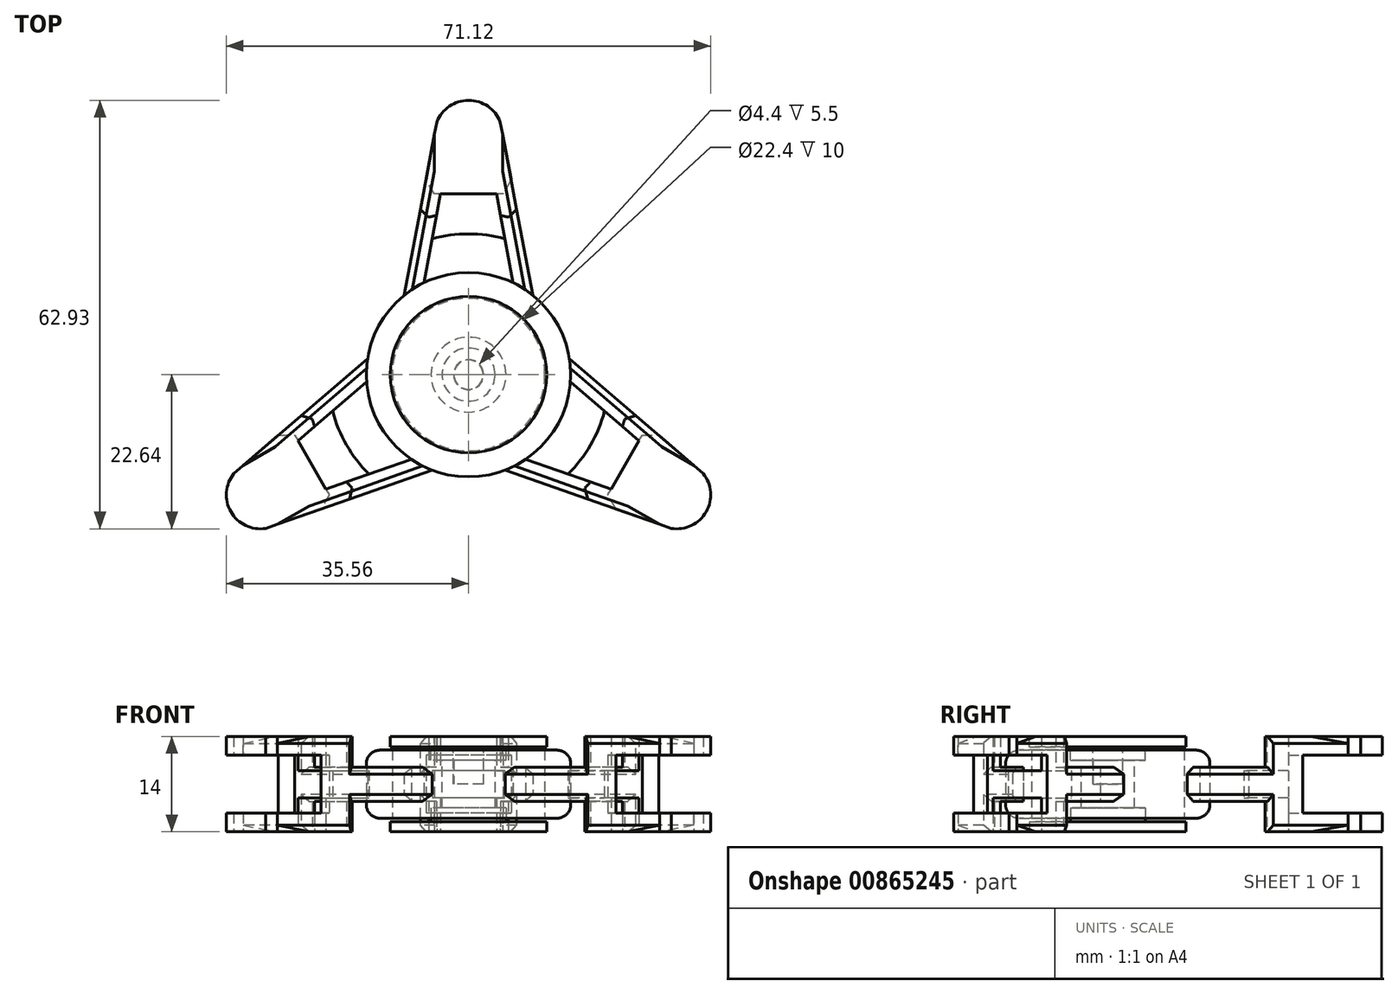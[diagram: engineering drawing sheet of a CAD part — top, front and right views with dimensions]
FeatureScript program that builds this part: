
annotation { "Feature Type Name" : "Feature", "Feature Type Description" : "" }
export const myFeature = defineFeature(function(context is Context, id is Id, definition is map)
    precondition{}
    {
        {
            var Q0;
            Q0=qCreatedBy(makeId("Top.planeOp"),FACE);
            var sketch = newSketch(context, id + "F0", { "sketchPlane" : qUnion([Q0])});
            skCircle(sketch, "E0", {"center": v(0, 0) * mm, "radius": 11.2 * mm});
            skCircle(sketch, "E1", {"center": v(0, 0) * mm, "radius": 15 * mm});
            skLineSegment(sketch, "E2.bottom", {"start": v(-1.99, 37.79) * mm, "end": v(1.99, 37.79) * mm});
            skLineSegment(sketch, "E2.top", {"start": v(-6.99, 11.2) * mm, "end": v(6.99, 11.2) * mm});
            skLineSegment(sketch, "E2.left", {"start": v(-1.99, 37.79) * mm, "end": v(-6.99, 11.2) * mm});
            skLineSegment(sketch, "E2.right", {"start": v(1.99, 37.79) * mm, "end": v(6.99, 11.2) * mm});
            skLineSegment(sketch, "E3.0", {"start": v(-4.06, 40.29) * mm, "end": v(-10, 8.7) * mm});
            skLineSegment(sketch, "E3.1", {"start": v(-4.06, 40.29) * mm, "end": v(4.06, 40.29) * mm});
            skLineSegment(sketch, "E3.2", {"start": v(4.06, 40.29) * mm, "end": v(10, 8.7) * mm});
            skLineSegment(sketch, "E3.3", {"start": v(-10, 8.7) * mm, "end": v(10, 8.7) * mm});
            skCircle(sketch, "E4", {"center": v(0, 0) * mm, "radius": 20.67 * mm});
            skCircle(sketch, "E5", {"center": v(0, 35.29) * mm, "radius": 5 * mm});
            skLineSegment(sketch, "E6", {"start": v(-30.4, 35.29) * mm, "end": v(24.87, 35.29) * mm});
            skCircle(sketch, "E7", {"center": v(0, 35.29) * mm, "radius": 2.3 * mm});
            skCircle(sketch, "E8", {"center": v(0, 35.29) * mm, "radius": 4.5 * mm});
            skCircle(sketch, "E9.cCircle", {"center": v(0, 35.29) * mm, "radius": 8.75 * mm, "construction": true});
            skLineSegment(sketch, "E9.0", {"start": v(10.1, 35.29) * mm, "end": v(5.05, 26.54) * mm});
            skLineSegment(sketch, "E9.1", {"start": v(5.05, 26.54) * mm, "end": v(-5.05, 26.54) * mm});
            skLineSegment(sketch, "E9.2", {"start": v(-5.05, 26.54) * mm, "end": v(-10.1, 35.29) * mm});
            skLineSegment(sketch, "E9.3", {"start": v(-10.1, 35.29) * mm, "end": v(-5.05, 44.04) * mm});
            skLineSegment(sketch, "E9.4", {"start": v(-5.05, 44.04) * mm, "end": v(5.05, 44.04) * mm});
            skLineSegment(sketch, "E9.5", {"start": v(5.05, 44.04) * mm, "end": v(10.1, 35.29) * mm});
            skPoint(sketch, "E9.0.midPoint", {"position": v(7.58, 30.91) * mm});
            skCircle(sketch, "E10", {"center": v(0, 0) * mm, "radius": 23.85 * mm});
            skCircle(sketch, "E11", {"center": v(0, 35.29) * mm, "radius": 3.2 * mm});
            skSolve(sketch);
        }
        {
            var Q0;
            {var subQ3=sQuery(id+"F0.wireOp",EDGE,"E0");Q0=makeQuery(id+"F0.imprint","IMPRINT",FACE,{"disambiguationData":[TD([[makeQuery(id+"F0.imprint","IMPRINT",EDGE,{"derivedFrom":subQ3}),-1.0]])]});}
            var Q1;
            {var subQ0=sQuery(id+"F0.wireOp",EDGE,"E2.left");var subQ3=sQuery(id+"F0.wireOp",EDGE,"E1");var subQ4=makeQuery(id+"F0.imprint","INTERSECT",VERTEX,{"derivedFrom":[subQ3,subQ0]});Q1=makeQuery(id+"F0.imprint","IMPRINT",FACE,{"disambiguationData":[TD([[makeQuery(id+"F0.imprint","IMPRINT",EDGE,{"disambiguationData":[TD([[subQ4,1.0]])],"derivedFrom":subQ3}),1.0]])]});}
            var Q2;
            {var subQ3=sQuery(id+"F0.wireOp",EDGE,"E1");var subQ6=sQuery(id+"F0.wireOp",EDGE,"c8613fa5-9237-46bb-8146-0ead7ceadabf.1.1");var subQ8=makeQuery(id+"F0.imprint","INTERSECT",VERTEX,{"derivedFrom":[subQ3,subQ6]});Q2=makeQuery(id+"F0.imprint","IMPRINT",FACE,{"disambiguationData":[TD([[makeQuery(id+"F0.imprint","IMPRINT",EDGE,{"disambiguationData":[TD([[subQ8,-1.0]])],"derivedFrom":subQ3}),1.0]])]});}
            var Q3;
            {var subQ3=sQuery(id+"F0.wireOp",EDGE,"E1");var subQ6=sQuery(id+"F0.wireOp",EDGE,"c8613fa5-9237-46bb-8146-0ead7ceadabf.2.1");var subQ8=makeQuery(id+"F0.imprint","INTERSECT",VERTEX,{"derivedFrom":[subQ3,subQ6]});Q3=makeQuery(id+"F0.imprint","IMPRINT",FACE,{"disambiguationData":[TD([[makeQuery(id+"F0.imprint","IMPRINT",EDGE,{"disambiguationData":[TD([[subQ8,-1.0]])],"derivedFrom":subQ3}),1.0]])]});}
            extrude(context, id + "F1", {"entities" : qUnion([Q0, Q1, Q2, Q3]), "endBound" : BoundingType.SYMMETRIC, "depth" : 10 * mm, "offsetDistance" : 25 * mm});
        }
        {
            var Q0;
            {var subQ0=sQuery(id+"F0.wireOp",EDGE,"E2.right");var subQ1=sQuery(id+"F0.wireOp",EDGE,"E1");var subQ2=makeQuery(id+"F0.imprint","INTERSECT",VERTEX,{"derivedFrom":[subQ1,subQ0]});Q0=makeQuery(id+"F0.imprint","IMPRINT",FACE,{"disambiguationData":[TD([[makeQuery(id+"F0.imprint","IMPRINT",EDGE,{"disambiguationData":[TD([[subQ2,1.0]])],"derivedFrom":subQ1}),-1.0]])]});}
            var Q1;
            {var subQ0=sQuery(id+"F0.wireOp",EDGE,"E2.left");var subQ1=sQuery(id+"F0.wireOp",EDGE,"E1");var subQ2=makeQuery(id+"F0.imprint","INTERSECT",VERTEX,{"derivedFrom":[subQ1,subQ0]});Q1=makeQuery(id+"F0.imprint","IMPRINT",FACE,{"disambiguationData":[TD([[makeQuery(id+"F0.imprint","IMPRINT",EDGE,{"disambiguationData":[TD([[subQ2,-1.0]])],"derivedFrom":subQ1}),-1.0]])]});}
            var Q2;
            {var subQ0=sQuery(id+"F0.wireOp",EDGE,"E10");var subQ1=sQuery(id+"F0.wireOp",EDGE,"E2.left");var subQ2=makeQuery(id+"F0.imprint","INTERSECT",VERTEX,{"derivedFrom":[subQ1,subQ0]});Q2=makeQuery(id+"F0.imprint","IMPRINT",FACE,{"disambiguationData":[TD([[makeQuery(id+"F0.imprint","IMPRINT",EDGE,{"disambiguationData":[TD([[subQ2,-1.0]])],"derivedFrom":subQ1}),-1.0]])]});}
            var Q3;
            {var subQ0=sQuery(id+"F0.wireOp",EDGE,"E10");var subQ1=sQuery(id+"F0.wireOp",EDGE,"E2.right");var subQ2=makeQuery(id+"F0.imprint","INTERSECT",VERTEX,{"derivedFrom":[subQ1,subQ0]});Q3=makeQuery(id+"F0.imprint","IMPRINT",FACE,{"disambiguationData":[TD([[makeQuery(id+"F0.imprint","IMPRINT",EDGE,{"disambiguationData":[TD([[subQ2,-1.0]])],"derivedFrom":subQ1}),1.0]])]});}
            extrude(context, id + "F2", {"entities" : qUnion([Q0, Q1, Q2, Q3]), "endBound" : BoundingType.SYMMETRIC, "depth" : 5 * mm, "offsetDistance" : 25 * mm});
        }
        {
            var Q0;
            {var subQ0=sQuery(id+"F0.wireOp",EDGE,"76ec63e9-d2f9-4aa1-b3ab-0722a41de434.2.0");var subQ1=sQuery(id+"F0.wireOp",EDGE,"c8613fa5-9237-46bb-8146-0ead7ceadabf.2.1");var subQ2=makeQuery(id+"F0.imprint","INTERSECT",VERTEX,{"derivedFrom":[subQ1,subQ0]});Q0=makeQuery(id+"F0.imprint","IMPRINT",FACE,{"disambiguationData":[TD([[makeQuery(id+"F0.imprint","IMPRINT",EDGE,{"disambiguationData":[TD([[subQ2,-1.0]])],"derivedFrom":subQ1}),-1.0]])]});}
            var Q1;
            {var subQ0=sQuery(id+"F0.wireOp",EDGE,"76ec63e9-d2f9-4aa1-b3ab-0722a41de434.1.0");var subQ1=sQuery(id+"F0.wireOp",EDGE,"c8613fa5-9237-46bb-8146-0ead7ceadabf.1.1");var subQ2=makeQuery(id+"F0.imprint","INTERSECT",VERTEX,{"derivedFrom":[subQ1,subQ0]});Q1=makeQuery(id+"F0.imprint","IMPRINT",FACE,{"disambiguationData":[TD([[makeQuery(id+"F0.imprint","IMPRINT",EDGE,{"disambiguationData":[TD([[subQ2,-1.0]])],"derivedFrom":subQ1}),-1.0]])]});}
            var Q2;
            {var subQ0=sQuery(id+"F0.wireOp",EDGE,"E9.1");var subQ1=sQuery(id+"F0.wireOp",EDGE,"E2.left");var subQ2=makeQuery(id+"F0.imprint","INTERSECT",VERTEX,{"derivedFrom":[subQ1,subQ0]});Q2=makeQuery(id+"F0.imprint","IMPRINT",FACE,{"disambiguationData":[TD([[makeQuery(id+"F0.imprint","IMPRINT",EDGE,{"disambiguationData":[TD([[subQ2,-1.0]])],"derivedFrom":subQ1}),1.0]])]});}
            var Q3;
            {var subQ0=sQuery(id+"F0.wireOp",EDGE,"E10");var subQ1=sQuery(id+"F0.wireOp",EDGE,"E2.left");var subQ2=makeQuery(id+"F0.imprint","INTERSECT",VERTEX,{"derivedFrom":[subQ1,subQ0]});Q3=makeQuery(id+"F0.imprint","IMPRINT",FACE,{"disambiguationData":[TD([[makeQuery(id+"F0.imprint","IMPRINT",EDGE,{"disambiguationData":[TD([[subQ2,-1.0]])],"derivedFrom":subQ1}),1.0]])]});}
            var Q4;
            {var subQ0=sQuery(id+"F0.wireOp",EDGE,"E10");var subQ1=sQuery(id+"F0.wireOp",EDGE,"c8613fa5-9237-46bb-8146-0ead7ceadabf.2.1");var subQ2=makeQuery(id+"F0.imprint","INTERSECT",VERTEX,{"derivedFrom":[subQ1,subQ0]});Q4=makeQuery(id+"F0.imprint","IMPRINT",FACE,{"disambiguationData":[TD([[makeQuery(id+"F0.imprint","IMPRINT",EDGE,{"disambiguationData":[TD([[subQ2,-1.0]])],"derivedFrom":subQ1}),-1.0]])]});}
            var Q5;
            {var subQ0=sQuery(id+"F0.wireOp",EDGE,"E10");var subQ1=sQuery(id+"F0.wireOp",EDGE,"c8613fa5-9237-46bb-8146-0ead7ceadabf.1.1");var subQ2=makeQuery(id+"F0.imprint","INTERSECT",VERTEX,{"derivedFrom":[subQ1,subQ0]});Q5=makeQuery(id+"F0.imprint","IMPRINT",FACE,{"disambiguationData":[TD([[makeQuery(id+"F0.imprint","IMPRINT",EDGE,{"disambiguationData":[TD([[subQ2,-1.0]])],"derivedFrom":subQ1}),-1.0]])]});}
            extrude(context, id + "F3", {"entities" : qUnion([Q0, Q1, Q2, Q3, Q4, Q5]), "operationType" : NewBodyOperationType.ADD, "endBound" : BoundingType.SYMMETRIC, "depth" : 4 * mm, "offsetDistance" : 25 * mm});
        }
        {
            var Q0;
            {var subQ0=sQuery(id+"F0.wireOp",EDGE,"E5");var subQ11=sQuery(id+"F0.wireOp",EDGE,"E3.0");var subQ12=makeQuery(id+"F0.imprint","INTERSECT",VERTEX,{"disambiguationData":[OD(0.0)],"derivedFrom":[subQ11,subQ0]});Q0=makeQuery(id+"F0.imprint","IMPRINT",FACE,{"disambiguationData":[TD([[makeQuery(id+"F0.imprint","IMPRINT",EDGE,{"disambiguationData":[TD([[subQ12,-1.0]])],"derivedFrom":subQ11}),1.0]])]});}
            var Q1;
            {var subQ5=sQuery(id+"F0.wireOp",EDGE,"E2.bottom");Q1=makeQuery(id+"F0.imprint","IMPRINT",FACE,{"disambiguationData":[TD([[makeQuery(id+"F0.imprint","IMPRINT",EDGE,{"derivedFrom":subQ5}),1.0]])]});}
            var Q2;
            {var subQ0=sQuery(id+"F0.wireOp",EDGE,"E6");var subQ1=sQuery(id+"F0.wireOp",EDGE,"E2.right");var subQ2=makeQuery(id+"F0.imprint","INTERSECT",VERTEX,{"derivedFrom":[subQ1,subQ0]});Q2=makeQuery(id+"F0.imprint","IMPRINT",FACE,{"disambiguationData":[TD([[makeQuery(id+"F0.imprint","IMPRINT",EDGE,{"disambiguationData":[TD([[subQ2,-1.0]])],"derivedFrom":subQ1}),1.0]])]});}
            var Q3;
            {var subQ0=sQuery(id+"F0.wireOp",EDGE,"E6");var subQ1=sQuery(id+"F0.wireOp",EDGE,"E2.left");var subQ2=makeQuery(id+"F0.imprint","INTERSECT",VERTEX,{"derivedFrom":[subQ1,subQ0]});Q3=makeQuery(id+"F0.imprint","IMPRINT",FACE,{"disambiguationData":[TD([[makeQuery(id+"F0.imprint","IMPRINT",EDGE,{"disambiguationData":[TD([[subQ2,-1.0]])],"derivedFrom":subQ1}),-1.0]])]});}
            var Q4;
            {var subQ0=sQuery(id+"F0.wireOp",EDGE,"E8");var subQ1=sQuery(id+"F0.wireOp",EDGE,"E2.left");var subQ2=makeQuery(id+"F0.imprint","INTERSECT",VERTEX,{"derivedFrom":[subQ1,subQ0]});Q4=makeQuery(id+"F0.imprint","IMPRINT",FACE,{"disambiguationData":[TD([[makeQuery(id+"F0.imprint","IMPRINT",EDGE,{"disambiguationData":[TD([[subQ2,-1.0]])],"derivedFrom":subQ1}),-1.0]])]});}
            var Q5;
            {var subQ0=sQuery(id+"F0.wireOp",EDGE,"E8");var subQ1=sQuery(id+"F0.wireOp",EDGE,"E2.left");var subQ2=makeQuery(id+"F0.imprint","INTERSECT",VERTEX,{"derivedFrom":[subQ1,subQ0]});Q5=makeQuery(id+"F0.imprint","IMPRINT",FACE,{"disambiguationData":[TD([[makeQuery(id+"F0.imprint","IMPRINT",EDGE,{"disambiguationData":[TD([[subQ2,-1.0]])],"derivedFrom":subQ1}),1.0]])]});}
            var Q6;
            {var subQ0=sQuery(id+"F0.wireOp",EDGE,"E6");var subQ1=sQuery(id+"F0.wireOp",EDGE,"E2.left");var subQ2=makeQuery(id+"F0.imprint","INTERSECT",VERTEX,{"derivedFrom":[subQ1,subQ0]});Q6=makeQuery(id+"F0.imprint","IMPRINT",FACE,{"disambiguationData":[TD([[makeQuery(id+"F0.imprint","IMPRINT",EDGE,{"disambiguationData":[TD([[subQ2,-1.0]])],"derivedFrom":subQ1}),1.0]])]});}
            var Q7;
            {var subQ0=sQuery(id+"F0.wireOp",EDGE,"E8");var subQ1=sQuery(id+"F0.wireOp",EDGE,"E2.right");var subQ2=makeQuery(id+"F0.imprint","INTERSECT",VERTEX,{"derivedFrom":[subQ1,subQ0]});Q7=makeQuery(id+"F0.imprint","IMPRINT",FACE,{"disambiguationData":[TD([[makeQuery(id+"F0.imprint","IMPRINT",EDGE,{"disambiguationData":[TD([[subQ2,-1.0]])],"derivedFrom":subQ1}),1.0]])]});}
            var Q8;
            {var subQ0=sQuery(id+"F0.wireOp",EDGE,"E5");var subQ1=sQuery(id+"F0.wireOp",EDGE,"E2.left");var subQ2=makeQuery(id+"F0.imprint","INTERSECT",VERTEX,{"derivedFrom":[subQ1,subQ0]});Q8=makeQuery(id+"F0.imprint","IMPRINT",FACE,{"disambiguationData":[TD([[makeQuery(id+"F0.imprint","IMPRINT",EDGE,{"disambiguationData":[TD([[subQ2,-1.0]])],"derivedFrom":subQ1}),-1.0]])]});}
            var Q9;
            {var subQ3=sQuery(id+"F0.wireOp",EDGE,"E5");var subQ5=sQuery(id+"F0.wireOp",EDGE,"E2.right");var subQ6=makeQuery(id+"F0.imprint","INTERSECT",VERTEX,{"derivedFrom":[subQ5,subQ3]});Q9=makeQuery(id+"F0.imprint","IMPRINT",FACE,{"disambiguationData":[TD([[makeQuery(id+"F0.imprint","IMPRINT",EDGE,{"disambiguationData":[TD([[subQ6,-1.0]])],"derivedFrom":subQ5}),1.0]])]});}
            var Q10;
            {var subQ1=sQuery(id+"F0.wireOp",EDGE,"E2.bottom");Q10=makeQuery(id+"F0.imprint","IMPRINT",FACE,{"disambiguationData":[TD([[makeQuery(id+"F0.imprint","IMPRINT",EDGE,{"derivedFrom":subQ1}),-1.0]])]});}
            var Q11;
            {var subQ1=sQuery(id+"F0.wireOp",EDGE,"E9.1");var subQ3=sQuery(id+"F0.wireOp",EDGE,"E2.left");var subQ4=makeQuery(id+"F0.imprint","INTERSECT",VERTEX,{"derivedFrom":[subQ3,subQ1]});Q11=makeQuery(id+"F0.imprint","IMPRINT",FACE,{"disambiguationData":[TD([[makeQuery(id+"F0.imprint","IMPRINT",EDGE,{"disambiguationData":[TD([[subQ4,-1.0]])],"derivedFrom":subQ3}),-1.0]])]});}
            var Q12;
            {var subQ0=sQuery(id+"F0.wireOp",EDGE,"E9.1");var subQ3=sQuery(id+"F0.wireOp",EDGE,"E2.right");var subQ4=makeQuery(id+"F0.imprint","INTERSECT",VERTEX,{"derivedFrom":[subQ3,subQ0]});Q12=makeQuery(id+"F0.imprint","IMPRINT",FACE,{"disambiguationData":[TD([[makeQuery(id+"F0.imprint","IMPRINT",EDGE,{"disambiguationData":[TD([[subQ4,-1.0]])],"derivedFrom":subQ3}),1.0]])]});}
            var Q13;
            {var subQ0=sQuery(id+"F0.wireOp",EDGE,"E5");var subQ1=sQuery(id+"F0.wireOp",EDGE,"E2.left");var subQ2=makeQuery(id+"F0.imprint","INTERSECT",VERTEX,{"derivedFrom":[subQ1,subQ0]});Q13=makeQuery(id+"F0.imprint","IMPRINT",FACE,{"disambiguationData":[TD([[makeQuery(id+"F0.imprint","IMPRINT",EDGE,{"disambiguationData":[TD([[subQ2,-1.0]])],"derivedFrom":subQ1}),1.0]])]});}
            var Q14;
            {var subQ0=sQuery(id+"F0.wireOp",EDGE,"E7");var subQ1=sQuery(id+"F0.wireOp",EDGE,"E6");var subQ2=makeQuery(id+"F0.imprint","INTERSECT",VERTEX,{"disambiguationData":[OD(0.0)],"derivedFrom":[subQ1,subQ0]});Q14=makeQuery(id+"F0.imprint","IMPRINT",FACE,{"disambiguationData":[TD([[makeQuery(id+"F0.imprint","IMPRINT",EDGE,{"disambiguationData":[TD([[subQ2,-1.0]])],"derivedFrom":subQ1}),-1.0]])]});}
            var Q15;
            {var subQ0=sQuery(id+"F0.wireOp",EDGE,"E7");var subQ1=sQuery(id+"F0.wireOp",EDGE,"E6");var subQ2=makeQuery(id+"F0.imprint","INTERSECT",VERTEX,{"disambiguationData":[OD(0.0)],"derivedFrom":[subQ1,subQ0]});Q15=makeQuery(id+"F0.imprint","IMPRINT",FACE,{"disambiguationData":[TD([[makeQuery(id+"F0.imprint","IMPRINT",EDGE,{"disambiguationData":[TD([[subQ2,-1.0]])],"derivedFrom":subQ1}),1.0]])]});}
            var Q16;
            {var subQ0=sQuery(id+"F0.wireOp",EDGE,"E11");var subQ1=sQuery(id+"F0.wireOp",EDGE,"E2.left");var subQ2=makeQuery(id+"F0.imprint","INTERSECT",VERTEX,{"derivedFrom":[subQ1,subQ0]});Q16=makeQuery(id+"F0.imprint","IMPRINT",FACE,{"disambiguationData":[TD([[makeQuery(id+"F0.imprint","IMPRINT",EDGE,{"disambiguationData":[TD([[subQ2,-1.0]])],"derivedFrom":subQ1}),1.0]])]});}
            var Q17;
            {var subQ0=sQuery(id+"F0.wireOp",EDGE,"E11");var subQ1=sQuery(id+"F0.wireOp",EDGE,"E2.right");var subQ2=makeQuery(id+"F0.imprint","INTERSECT",VERTEX,{"derivedFrom":[subQ1,subQ0]});Q17=makeQuery(id+"F0.imprint","IMPRINT",FACE,{"disambiguationData":[TD([[makeQuery(id+"F0.imprint","IMPRINT",EDGE,{"disambiguationData":[TD([[subQ2,-1.0]])],"derivedFrom":subQ1}),1.0]])]});}
            var Q18;
            {var subQ0=sQuery(id+"F0.wireOp",EDGE,"E8");var subQ1=sQuery(id+"F0.wireOp",EDGE,"E6");var subQ2=makeQuery(id+"F0.imprint","INTERSECT",VERTEX,{"disambiguationData":[OD(0.0)],"derivedFrom":[subQ1,subQ0]});Q18=makeQuery(id+"F0.imprint","IMPRINT",FACE,{"disambiguationData":[TD([[makeQuery(id+"F0.imprint","IMPRINT",EDGE,{"disambiguationData":[TD([[subQ2,-1.0]])],"derivedFrom":subQ1}),1.0]])]});}
            var Q19;
            {var subQ0=sQuery(id+"F0.wireOp",EDGE,"E11");var subQ1=sQuery(id+"F0.wireOp",EDGE,"E2.left");var subQ2=makeQuery(id+"F0.imprint","INTERSECT",VERTEX,{"derivedFrom":[subQ1,subQ0]});Q19=makeQuery(id+"F0.imprint","IMPRINT",FACE,{"disambiguationData":[TD([[makeQuery(id+"F0.imprint","IMPRINT",EDGE,{"disambiguationData":[TD([[subQ2,-1.0]])],"derivedFrom":subQ1}),-1.0]])]});}
            extrude(context, id + "F4", {"entities" : qUnion([Q0, Q1, Q2, Q3, Q4, Q5, Q6, Q7, Q8, Q9, Q10, Q11, Q12, Q13, Q14, Q15, Q16, Q17, Q18, Q19]), "operationType" : NewBodyOperationType.ADD, "endBound" : BoundingType.SYMMETRIC, "depth" : 14 * mm, "offsetDistance" : 25 * mm});
        }
        {
            var Q0;
            {var subQ0=sQuery(id+"F0.wireOp",EDGE,"E9.3");Q0=makeQuery(id+"F0.imprint","IMPRINT",FACE,{"disambiguationData":[TD([[makeQuery(id+"F0.imprint","IMPRINT",EDGE,{"derivedFrom":subQ0}),-1.0]])]});}
            var Q1;
            {var subQ0=sQuery(id+"F0.wireOp",EDGE,"E9.0");var subQ1=sQuery(id+"F0.wireOp",EDGE,"E3.2");var subQ2=makeQuery(id+"F0.imprint","INTERSECT",VERTEX,{"derivedFrom":[subQ1,subQ0]});Q1=makeQuery(id+"F0.imprint","IMPRINT",FACE,{"disambiguationData":[TD([[makeQuery(id+"F0.imprint","IMPRINT",EDGE,{"disambiguationData":[TD([[subQ2,1.0]])],"derivedFrom":subQ1}),1.0]])]});}
            var Q2;
            {var subQ5=sQuery(id+"F0.wireOp",EDGE,"E2.bottom");Q2=makeQuery(id+"F0.imprint","IMPRINT",FACE,{"disambiguationData":[TD([[makeQuery(id+"F0.imprint","IMPRINT",EDGE,{"derivedFrom":subQ5}),1.0]])]});}
            var Q3;
            {var subQ0=sQuery(id+"F0.wireOp",EDGE,"E5");var subQ1=sQuery(id+"F0.wireOp",EDGE,"E2.left");var subQ2=makeQuery(id+"F0.imprint","INTERSECT",VERTEX,{"derivedFrom":[subQ1,subQ0]});Q3=makeQuery(id+"F0.imprint","IMPRINT",FACE,{"disambiguationData":[TD([[makeQuery(id+"F0.imprint","IMPRINT",EDGE,{"disambiguationData":[TD([[subQ2,-1.0]])],"derivedFrom":subQ1}),-1.0]])]});}
            var Q4;
            {var subQ0=sQuery(id+"F0.wireOp",EDGE,"E5");var subQ1=sQuery(id+"F0.wireOp",EDGE,"E2.left");var subQ2=makeQuery(id+"F0.imprint","INTERSECT",VERTEX,{"derivedFrom":[subQ1,subQ0]});Q4=makeQuery(id+"F0.imprint","IMPRINT",FACE,{"disambiguationData":[TD([[makeQuery(id+"F0.imprint","IMPRINT",EDGE,{"disambiguationData":[TD([[subQ2,-1.0]])],"derivedFrom":subQ1}),1.0]])]});}
            var Q5;
            {var subQ0=sQuery(id+"F0.wireOp",EDGE,"E7");var subQ1=sQuery(id+"F0.wireOp",EDGE,"E6");var subQ2=makeQuery(id+"F0.imprint","INTERSECT",VERTEX,{"disambiguationData":[OD(0.0)],"derivedFrom":[subQ1,subQ0]});Q5=makeQuery(id+"F0.imprint","IMPRINT",FACE,{"disambiguationData":[TD([[makeQuery(id+"F0.imprint","IMPRINT",EDGE,{"disambiguationData":[TD([[subQ2,-1.0]])],"derivedFrom":subQ1}),-1.0]])]});}
            var Q6;
            {var subQ0=sQuery(id+"F0.wireOp",EDGE,"E7");var subQ1=sQuery(id+"F0.wireOp",EDGE,"E6");var subQ2=makeQuery(id+"F0.imprint","INTERSECT",VERTEX,{"disambiguationData":[OD(0.0)],"derivedFrom":[subQ1,subQ0]});Q6=makeQuery(id+"F0.imprint","IMPRINT",FACE,{"disambiguationData":[TD([[makeQuery(id+"F0.imprint","IMPRINT",EDGE,{"disambiguationData":[TD([[subQ2,-1.0]])],"derivedFrom":subQ1}),1.0]])]});}
            var Q7;
            {var subQ0=sQuery(id+"F0.wireOp",EDGE,"E3.1");var subQ1=sQuery(id+"F0.wireOp",EDGE,"E3.0");var subQ2=makeQuery(id+"F0.imprint","INTERSECT",VERTEX,{"derivedFrom":[subQ1,subQ0]});Q7=makeQuery(id+"F0.imprint","IMPRINT",FACE,{"disambiguationData":[TD([[makeQuery(id+"F0.imprint","IMPRINT",EDGE,{"disambiguationData":[TD([[subQ2,-1.0]])],"derivedFrom":subQ1}),1.0]])]});}
            var Q8;
            {var subQ0=sQuery(id+"F0.wireOp",EDGE,"E3.2");var subQ1=sQuery(id+"F0.wireOp",EDGE,"E3.1");var subQ2=makeQuery(id+"F0.imprint","INTERSECT",VERTEX,{"derivedFrom":[subQ1,subQ0]});Q8=makeQuery(id+"F0.imprint","IMPRINT",FACE,{"disambiguationData":[TD([[makeQuery(id+"F0.imprint","IMPRINT",EDGE,{"disambiguationData":[TD([[subQ2,1.0]])],"derivedFrom":subQ1}),-1.0]])]});}
            var Q9;
            {var subQ3=sQuery(id+"F0.wireOp",EDGE,"E5");var subQ5=sQuery(id+"F0.wireOp",EDGE,"E2.right");var subQ6=makeQuery(id+"F0.imprint","INTERSECT",VERTEX,{"derivedFrom":[subQ5,subQ3]});Q9=makeQuery(id+"F0.imprint","IMPRINT",FACE,{"disambiguationData":[TD([[makeQuery(id+"F0.imprint","IMPRINT",EDGE,{"disambiguationData":[TD([[subQ6,-1.0]])],"derivedFrom":subQ5}),1.0]])]});}
            var Q10;
            {var subQ0=sQuery(id+"F0.wireOp",EDGE,"E8");var subQ1=sQuery(id+"F0.wireOp",EDGE,"E2.left");var subQ2=makeQuery(id+"F0.imprint","INTERSECT",VERTEX,{"derivedFrom":[subQ1,subQ0]});Q10=makeQuery(id+"F0.imprint","IMPRINT",FACE,{"disambiguationData":[TD([[makeQuery(id+"F0.imprint","IMPRINT",EDGE,{"disambiguationData":[TD([[subQ2,-1.0]])],"derivedFrom":subQ1}),1.0]])]});}
            var Q11;
            {var subQ0=sQuery(id+"F0.wireOp",EDGE,"E8");var subQ1=sQuery(id+"F0.wireOp",EDGE,"E2.right");var subQ2=makeQuery(id+"F0.imprint","INTERSECT",VERTEX,{"derivedFrom":[subQ1,subQ0]});Q11=makeQuery(id+"F0.imprint","IMPRINT",FACE,{"disambiguationData":[TD([[makeQuery(id+"F0.imprint","IMPRINT",EDGE,{"disambiguationData":[TD([[subQ2,-1.0]])],"derivedFrom":subQ1}),1.0]])]});}
            var Q12;
            {var subQ0=sQuery(id+"F0.wireOp",EDGE,"E6");var subQ1=sQuery(id+"F0.wireOp",EDGE,"E2.right");var subQ2=makeQuery(id+"F0.imprint","INTERSECT",VERTEX,{"derivedFrom":[subQ1,subQ0]});Q12=makeQuery(id+"F0.imprint","IMPRINT",FACE,{"disambiguationData":[TD([[makeQuery(id+"F0.imprint","IMPRINT",EDGE,{"disambiguationData":[TD([[subQ2,-1.0]])],"derivedFrom":subQ1}),1.0]])]});}
            var Q13;
            {var subQ0=sQuery(id+"F0.wireOp",EDGE,"E6");var subQ1=sQuery(id+"F0.wireOp",EDGE,"E2.left");var subQ2=makeQuery(id+"F0.imprint","INTERSECT",VERTEX,{"derivedFrom":[subQ1,subQ0]});Q13=makeQuery(id+"F0.imprint","IMPRINT",FACE,{"disambiguationData":[TD([[makeQuery(id+"F0.imprint","IMPRINT",EDGE,{"disambiguationData":[TD([[subQ2,-1.0]])],"derivedFrom":subQ1}),1.0]])]});}
            var Q14;
            {var subQ0=sQuery(id+"F0.wireOp",EDGE,"E8");var subQ1=sQuery(id+"F0.wireOp",EDGE,"E2.left");var subQ2=makeQuery(id+"F0.imprint","INTERSECT",VERTEX,{"derivedFrom":[subQ1,subQ0]});Q14=makeQuery(id+"F0.imprint","IMPRINT",FACE,{"disambiguationData":[TD([[makeQuery(id+"F0.imprint","IMPRINT",EDGE,{"disambiguationData":[TD([[subQ2,-1.0]])],"derivedFrom":subQ1}),-1.0]])]});}
            var Q15;
            {var subQ0=sQuery(id+"F0.wireOp",EDGE,"E6");var subQ1=sQuery(id+"F0.wireOp",EDGE,"E2.left");var subQ2=makeQuery(id+"F0.imprint","INTERSECT",VERTEX,{"derivedFrom":[subQ1,subQ0]});Q15=makeQuery(id+"F0.imprint","IMPRINT",FACE,{"disambiguationData":[TD([[makeQuery(id+"F0.imprint","IMPRINT",EDGE,{"disambiguationData":[TD([[subQ2,-1.0]])],"derivedFrom":subQ1}),-1.0]])]});}
            var Q16;
            {var subQ0=sQuery(id+"F0.wireOp",EDGE,"E5");var subQ11=sQuery(id+"F0.wireOp",EDGE,"E3.0");var subQ12=makeQuery(id+"F0.imprint","INTERSECT",VERTEX,{"disambiguationData":[OD(0.0)],"derivedFrom":[subQ11,subQ0]});Q16=makeQuery(id+"F0.imprint","IMPRINT",FACE,{"disambiguationData":[TD([[makeQuery(id+"F0.imprint","IMPRINT",EDGE,{"disambiguationData":[TD([[subQ12,-1.0]])],"derivedFrom":subQ11}),1.0]])]});}
            var Q17;
            {var subQ0=sQuery(id+"F0.wireOp",EDGE,"E5");var subQ1=sQuery(id+"F0.wireOp",EDGE,"E3.2");var subQ2=makeQuery(id+"F0.imprint","INTERSECT",VERTEX,{"disambiguationData":[OD(0.0)],"derivedFrom":[subQ1,subQ0]});Q17=makeQuery(id+"F0.imprint","IMPRINT",FACE,{"disambiguationData":[TD([[makeQuery(id+"F0.imprint","IMPRINT",EDGE,{"disambiguationData":[TD([[subQ2,-1.0]])],"derivedFrom":subQ1}),1.0]])]});}
            var Q18;
            {var subQ1=sQuery(id+"F0.wireOp",EDGE,"E2.bottom");Q18=makeQuery(id+"F0.imprint","IMPRINT",FACE,{"disambiguationData":[TD([[makeQuery(id+"F0.imprint","IMPRINT",EDGE,{"derivedFrom":subQ1}),-1.0]])]});}
            var Q19;
            {var subQ0=sQuery(id+"F0.wireOp",EDGE,"E5");var subQ1=sQuery(id+"F0.wireOp",EDGE,"E3.0");var subQ2=makeQuery(id+"F0.imprint","INTERSECT",VERTEX,{"disambiguationData":[OD(0.0)],"derivedFrom":[subQ1,subQ0]});Q19=makeQuery(id+"F0.imprint","IMPRINT",FACE,{"disambiguationData":[TD([[makeQuery(id+"F0.imprint","IMPRINT",EDGE,{"disambiguationData":[TD([[subQ2,-1.0]])],"derivedFrom":subQ1}),-1.0]])]});}
            var Q20;
            {var subQ0=sQuery(id+"F0.wireOp",EDGE,"E9.2");var subQ1=sQuery(id+"F0.wireOp",EDGE,"E3.0");var subQ2=makeQuery(id+"F0.imprint","INTERSECT",VERTEX,{"derivedFrom":[subQ1,subQ0]});Q20=makeQuery(id+"F0.imprint","IMPRINT",FACE,{"disambiguationData":[TD([[makeQuery(id+"F0.imprint","IMPRINT",EDGE,{"disambiguationData":[TD([[subQ2,1.0]])],"derivedFrom":subQ1}),-1.0]])]});}
            var Q21;
            {var subQ0=sQuery(id+"F0.wireOp",EDGE,"E11");var subQ1=sQuery(id+"F0.wireOp",EDGE,"E2.left");var subQ2=makeQuery(id+"F0.imprint","INTERSECT",VERTEX,{"derivedFrom":[subQ1,subQ0]});Q21=makeQuery(id+"F0.imprint","IMPRINT",FACE,{"disambiguationData":[TD([[makeQuery(id+"F0.imprint","IMPRINT",EDGE,{"disambiguationData":[TD([[subQ2,-1.0]])],"derivedFrom":subQ1}),-1.0]])]});}
            var Q22;
            {var subQ0=sQuery(id+"F0.wireOp",EDGE,"E11");var subQ1=sQuery(id+"F0.wireOp",EDGE,"E2.right");var subQ2=makeQuery(id+"F0.imprint","INTERSECT",VERTEX,{"derivedFrom":[subQ1,subQ0]});Q22=makeQuery(id+"F0.imprint","IMPRINT",FACE,{"disambiguationData":[TD([[makeQuery(id+"F0.imprint","IMPRINT",EDGE,{"disambiguationData":[TD([[subQ2,-1.0]])],"derivedFrom":subQ1}),1.0]])]});}
            var Q23;
            {var subQ0=sQuery(id+"F0.wireOp",EDGE,"E11");var subQ1=sQuery(id+"F0.wireOp",EDGE,"E2.left");var subQ2=makeQuery(id+"F0.imprint","INTERSECT",VERTEX,{"derivedFrom":[subQ1,subQ0]});Q23=makeQuery(id+"F0.imprint","IMPRINT",FACE,{"disambiguationData":[TD([[makeQuery(id+"F0.imprint","IMPRINT",EDGE,{"disambiguationData":[TD([[subQ2,-1.0]])],"derivedFrom":subQ1}),1.0]])]});}
            var Q24;
            {var subQ0=sQuery(id+"F0.wireOp",EDGE,"E8");var subQ1=sQuery(id+"F0.wireOp",EDGE,"E6");var subQ2=makeQuery(id+"F0.imprint","INTERSECT",VERTEX,{"disambiguationData":[OD(0.0)],"derivedFrom":[subQ1,subQ0]});Q24=makeQuery(id+"F0.imprint","IMPRINT",FACE,{"disambiguationData":[TD([[makeQuery(id+"F0.imprint","IMPRINT",EDGE,{"disambiguationData":[TD([[subQ2,-1.0]])],"derivedFrom":subQ1}),1.0]])]});}
            extrude(context, id + "F5", {"entities" : qUnion([Q0, Q1, Q2, Q3, Q4, Q5, Q6, Q7, Q8, Q9, Q10, Q11, Q12, Q13, Q14, Q15, Q16, Q17, Q18, Q19, Q20, Q21, Q22, Q23, Q24]), "operationType" : NewBodyOperationType.REMOVE, "endBound" : BoundingType.SYMMETRIC, "depth" : 8.5 * mm, "offsetDistance" : 25 * mm});
        }
        {
            var Q0;
            Q0=makeQuery(id+"F1.opExtrude","CAP_EDGE",EDGE,{"disambiguationData":[OSD([sQuery(id+"F0.wireOp",EDGE,"E1")])],"isStart":false});
            var Q1;
            Q1=makeQuery(id+"F1.opExtrude","CAP_EDGE",EDGE,{"disambiguationData":[OSD([sQuery(id+"F0.wireOp",EDGE,"E1")])],"isStart":true});
            fillet(context, id + "F6", {"entities" : qUnion([Q0, Q1]), "radius" : 2 * mm, "tangentPropagation" : true, "allowEdgeOverflow" : false});
        }
        {
            var Q0;
            {var subQ0=sQuery(id+"F0.wireOp",EDGE,"E3.0");var subQ1=makeQuery(id+"F0.imprint","INTERSECT",VERTEX,{"derivedFrom":[subQ0,sQuery(id+"F0.wireOp",EDGE,"E9.2")]});Q0=makeQuery(id+"F4.opExtrude","CAP_EDGE",EDGE,{"disambiguationData":[OSD([subQ0]),TDD([makeQuery(id+"F0.imprint","IMPRINT",EDGE,{"disambiguationData":[TD([[subQ1,1.0]])],"derivedFrom":subQ0}),makeQuery(id+"F0.imprint","IMPRINT",EDGE,{"disambiguationData":[TD([[subQ1,-1.0]])],"derivedFrom":subQ0})])],"isStart":false});}
            var Q1;
            {var subQ0=sQuery(id+"F0.wireOp",EDGE,"E3.2");var subQ1=makeQuery(id+"F0.imprint","INTERSECT",VERTEX,{"derivedFrom":[subQ0,sQuery(id+"F0.wireOp",EDGE,"E9.0")]});Q1=makeQuery(id+"F4.opExtrude","CAP_EDGE",EDGE,{"disambiguationData":[OSD([subQ0]),TDD([makeQuery(id+"F0.imprint","IMPRINT",EDGE,{"disambiguationData":[TD([[subQ1,1.0]])],"derivedFrom":subQ0}),makeQuery(id+"F0.imprint","IMPRINT",EDGE,{"disambiguationData":[TD([[subQ1,-1.0]])],"derivedFrom":subQ0})])],"isStart":false});}
            var Q2;
            Q2=makeQuery(id+"F2.opExtrude","CAP_EDGE",EDGE,{"disambiguationData":[OSD([sQuery(id+"F0.wireOp",EDGE,"E3.0")])],"isStart":false});
            var Q3;
            {var subQ0=sQuery(id+"F0.wireOp",EDGE,"E3.0");var subQ2=sQuery(id+"F0.wireOp",EDGE,"E10");var subQ5=sQuery(id+"F0.wireOp",EDGE,"E2.left");Q3=makeQuery(id+"F4.boolean.opBoolean","SPLIT",EDGE,{"disambiguationData":[TD([makeQuery(id+"F2.opExtrude","CAP_FACE",FACE,{"disambiguationData":[OSD([sQuery(id+"F0.wireOp",EDGE,"E1"),subQ5,subQ0,subQ2])],"isStart":false})])],"derivedFrom":makeQuery(id+"F4.opExtrude","SWEPT_EDGE",EDGE,{"disambiguationData":[OSD([subQ0,subQ2])]})});}
            var Q4;
            {var subQ0=sQuery(id+"F0.wireOp",EDGE,"E3.2");var subQ2=sQuery(id+"F0.wireOp",EDGE,"E10");var subQ5=sQuery(id+"F0.wireOp",EDGE,"E2.right");Q4=makeQuery(id+"F4.boolean.opBoolean","SPLIT",EDGE,{"disambiguationData":[TD([makeQuery(id+"F2.opExtrude","CAP_FACE",FACE,{"disambiguationData":[OSD([sQuery(id+"F0.wireOp",EDGE,"E1"),subQ5,subQ0,subQ2])],"isStart":false})])],"derivedFrom":makeQuery(id+"F4.opExtrude","SWEPT_EDGE",EDGE,{"disambiguationData":[OSD([subQ0,subQ2])]})});}
            var Q5;
            Q5=makeQuery(id+"F2.opExtrude","CAP_EDGE",EDGE,{"disambiguationData":[OSD([sQuery(id+"F0.wireOp",EDGE,"E3.2")])],"isStart":false});
            var Q6;
            Q6=makeQuery(id+"F2.opExtrude","CAP_EDGE",EDGE,{"disambiguationData":[OSD([sQuery(id+"F0.wireOp",EDGE,"E3.2")])],"isStart":true});
            var Q7;
            {var subQ0=sQuery(id+"F0.wireOp",EDGE,"E3.2");var subQ2=sQuery(id+"F0.wireOp",EDGE,"E10");var subQ5=sQuery(id+"F0.wireOp",EDGE,"E2.right");Q7=makeQuery(id+"F4.boolean.opBoolean","SPLIT",EDGE,{"disambiguationData":[TD([makeQuery(id+"F2.opExtrude","CAP_FACE",FACE,{"disambiguationData":[OSD([sQuery(id+"F0.wireOp",EDGE,"E1"),subQ5,subQ0,subQ2])],"isStart":true})])],"derivedFrom":makeQuery(id+"F4.opExtrude","SWEPT_EDGE",EDGE,{"disambiguationData":[OSD([subQ0,subQ2])]})});}
            var Q8;
            {var subQ0=sQuery(id+"F0.wireOp",EDGE,"E3.2");var subQ1=makeQuery(id+"F0.imprint","INTERSECT",VERTEX,{"derivedFrom":[subQ0,sQuery(id+"F0.wireOp",EDGE,"E9.0")]});Q8=makeQuery(id+"F4.opExtrude","CAP_EDGE",EDGE,{"disambiguationData":[OSD([subQ0]),TDD([makeQuery(id+"F0.imprint","IMPRINT",EDGE,{"disambiguationData":[TD([[subQ1,1.0]])],"derivedFrom":subQ0}),makeQuery(id+"F0.imprint","IMPRINT",EDGE,{"disambiguationData":[TD([[subQ1,-1.0]])],"derivedFrom":subQ0})])],"isStart":true});}
            var Q9;
            {var subQ0=sQuery(id+"F0.wireOp",EDGE,"E3.0");var subQ1=makeQuery(id+"F0.imprint","INTERSECT",VERTEX,{"derivedFrom":[subQ0,sQuery(id+"F0.wireOp",EDGE,"E9.2")]});Q9=makeQuery(id+"F4.opExtrude","CAP_EDGE",EDGE,{"disambiguationData":[OSD([subQ0]),TDD([makeQuery(id+"F0.imprint","IMPRINT",EDGE,{"disambiguationData":[TD([[subQ1,1.0]])],"derivedFrom":subQ0}),makeQuery(id+"F0.imprint","IMPRINT",EDGE,{"disambiguationData":[TD([[subQ1,-1.0]])],"derivedFrom":subQ0})])],"isStart":true});}
            var Q10;
            {var subQ0=sQuery(id+"F0.wireOp",EDGE,"E3.0");var subQ2=sQuery(id+"F0.wireOp",EDGE,"E10");var subQ5=sQuery(id+"F0.wireOp",EDGE,"E2.left");Q10=makeQuery(id+"F4.boolean.opBoolean","SPLIT",EDGE,{"disambiguationData":[TD([makeQuery(id+"F2.opExtrude","CAP_FACE",FACE,{"disambiguationData":[OSD([sQuery(id+"F0.wireOp",EDGE,"E1"),subQ5,subQ0,subQ2])],"isStart":true})])],"derivedFrom":makeQuery(id+"F4.opExtrude","SWEPT_EDGE",EDGE,{"disambiguationData":[OSD([subQ0,subQ2])]})});}
            var Q11;
            Q11=makeQuery(id+"F2.opExtrude","CAP_EDGE",EDGE,{"disambiguationData":[OSD([sQuery(id+"F0.wireOp",EDGE,"E3.0")])],"isStart":true});
            chamfer(context, id + "F7", {"entities" : qUnion([Q0, Q1, Q2, Q3, Q4, Q5, Q6, Q7, Q8, Q9, Q10, Q11]), "width" : 1 * mm, "tangentPropagation" : true});
        }
        {
            var Q0;
            Q0=qCreatedBy(makeId("Top.planeOp"),FACE);
            cPlane(context, id + "F8", {"entities" : qUnion([Q0]), "cplaneType" : CPlaneType.OFFSET, "offset" : 7 * mm, "width" : 150 * mm, "height" : 150 * mm});
        }
        {
            var Q0;
            Q0=qCreatedBy(makeId("Top.planeOp"),FACE);
            cPlane(context, id + "F9", {"entities" : qUnion([Q0]), "cplaneType" : CPlaneType.OFFSET, "offset" : 7 * mm, "oppositeDirection" : true, "width" : 150 * mm, "height" : 150 * mm});
        }
        {
            var Q0;
            Q0=qCreatedBy(id+"F8.planeOp",FACE);
            var sketch = newSketch(context, id + "F10", { "sketchPlane" : qUnion([Q0])});
            skCircle(sketch, "E12", {"center": v(0, 0) * mm, "radius": 11.5 * mm});
            skCircle(sketch, "E13", {"center": v(0, 0) * mm, "radius": 3.9 * mm});
            skCircle(sketch, "E14", {"center": v(0, 0) * mm, "radius": 2.05 * mm});
            skCircle(sketch, "E15", {"center": v(0, 0) * mm, "radius": 2.2 * mm});
            skCircle(sketch, "E16", {"center": v(0, 35.3) * mm, "radius": 4.5 * mm});
            skCircle(sketch, "E17", {"center": v(0, 35.3) * mm, "radius": 3.38 * mm});
            skCircle(sketch, "E18", {"center": v(0, 0) * mm, "radius": 5.5 * mm});
            skSolve(sketch);
        }
        {
            var Q0;
            Q0=makeQuery(id+"F10.imprint","IMPRINT",FACE,{"disambiguationData":[TD([[makeQuery(id+"F10.imprint","IMPRINT",EDGE,{"derivedFrom":sQuery(id+"F10.wireOp",EDGE,"E12")}),1.0]])]});
            var Q1;
            Q1=makeQuery(id+"F10.imprint","IMPRINT",FACE,{"disambiguationData":[TD([[makeQuery(id+"F10.imprint","IMPRINT",EDGE,{"derivedFrom":sQuery(id+"F10.wireOp",EDGE,"E13")}),1.0]])]});
            var Q2;
            Q2=makeQuery(id+"F10.imprint","IMPRINT",FACE,{"disambiguationData":[TD([[makeQuery(id+"F10.imprint","IMPRINT",EDGE,{"derivedFrom":sQuery(id+"F10.wireOp",EDGE,"E14")}),1.0]])]});
            var Q3;
            Q3=makeQuery(id+"F10.imprint","IMPRINT",FACE,{"disambiguationData":[TD([[makeQuery(id+"F10.imprint","IMPRINT",EDGE,{"derivedFrom":sQuery(id+"F10.wireOp",EDGE,"E14")}),-1.0]])]});
            var Q4;
            Q4=makeQuery(id+"F10.imprint","IMPRINT",FACE,{"disambiguationData":[TD([[makeQuery(id+"F10.imprint","IMPRINT",EDGE,{"derivedFrom":sQuery(id+"F10.wireOp",EDGE,"E13")}),-1.0]])]});
            var Q5;
            Q5=sQuery(id+"F10.wireOp",EDGE,"E12");
            extrude(context, id + "F11", {"entities" : qUnion([Q0, Q1, Q2, Q3, Q4]), "surfaceEntities" : qUnion([Q5]), "oppositeDirection" : true, "depth" : 1.5 * mm, "offsetDistance" : 25 * mm});
        }
        {
            var Q0;
            Q0=qCreatedBy(id+"F9.planeOp",FACE);
            var sketch = newSketch(context, id + "F12", { "sketchPlane" : qUnion([Q0])});
            skCircle(sketch, "E19", {"center": v(0, 0) * mm, "radius": 11.5 * mm});
            skCircle(sketch, "E20", {"center": v(0, 0) * mm, "radius": 3.9 * mm});
            skCircle(sketch, "E21", {"center": v(0, 0) * mm, "radius": 2.15 * mm});
            skCircle(sketch, "E22", {"center": v(0.01, 35.31) * mm, "radius": 4.5 * mm});
            skCircle(sketch, "E23", {"center": v(0.01, 35.31) * mm, "radius": 3.38 * mm});
            skCircle(sketch, "E24", {"center": v(0, 0) * mm, "radius": 2.05 * mm});
            skCircle(sketch, "E25", {"center": v(0, 0) * mm, "radius": 5.5 * mm});
            skSolve(sketch);
        }
        {
            var Q0;
            Q0=makeQuery(id+"F12.imprint","IMPRINT",FACE,{"disambiguationData":[TD([[makeQuery(id+"F12.imprint","IMPRINT",EDGE,{"derivedFrom":sQuery(id+"F12.wireOp",EDGE,"E19")}),1.0]])]});
            var Q1;
            Q1=makeQuery(id+"F12.imprint","IMPRINT",FACE,{"disambiguationData":[TD([[makeQuery(id+"F12.imprint","IMPRINT",EDGE,{"derivedFrom":sQuery(id+"F12.wireOp",EDGE,"E20")}),1.0]])]});
            var Q2;
            Q2=makeQuery(id+"F12.imprint","IMPRINT",FACE,{"disambiguationData":[TD([[makeQuery(id+"F12.imprint","IMPRINT",EDGE,{"derivedFrom":sQuery(id+"F12.wireOp",EDGE,"E24")}),1.0]])]});
            var Q3;
            Q3=makeQuery(id+"F12.imprint","IMPRINT",FACE,{"disambiguationData":[TD([[makeQuery(id+"F12.imprint","IMPRINT",EDGE,{"derivedFrom":sQuery(id+"F12.wireOp",EDGE,"E21")}),1.0]])]});
            var Q4;
            Q4=makeQuery(id+"F12.imprint","IMPRINT",FACE,{"disambiguationData":[TD([[makeQuery(id+"F12.imprint","IMPRINT",EDGE,{"derivedFrom":sQuery(id+"F12.wireOp",EDGE,"E20")}),-1.0]])]});
            extrude(context, id + "F13", {"entities" : qUnion([Q0, Q1, Q2, Q3, Q4]), "depth" : 1.5 * mm, "offsetDistance" : 25 * mm});
        }
        {
            var Q0;
            Q0=makeQuery(id+"F10.imprint","IMPRINT",FACE,{"disambiguationData":[TD([[makeQuery(id+"F10.imprint","IMPRINT",EDGE,{"derivedFrom":sQuery(id+"F10.wireOp",EDGE,"E13")}),1.0]])]});
            extrude(context, id + "F14", {"entities" : qUnion([Q0]), "operationType" : NewBodyOperationType.ADD, "oppositeDirection" : true, "depth" : 7 * mm, "offsetDistance" : 25 * mm});
        }
        {
            var Q0;
            Q0=makeQuery(id+"F12.imprint","IMPRINT",FACE,{"disambiguationData":[TD([[makeQuery(id+"F12.imprint","IMPRINT",EDGE,{"derivedFrom":sQuery(id+"F12.wireOp",EDGE,"E21")}),1.0]])]});
            var Q1;
            Q1=makeQuery(id+"F12.imprint","IMPRINT",FACE,{"disambiguationData":[TD([[makeQuery(id+"F12.imprint","IMPRINT",EDGE,{"derivedFrom":sQuery(id+"F12.wireOp",EDGE,"E24")}),1.0]])]});
            var Q2;
            Q2=sQuery(id+"F12.wireOp",EDGE,"E21");
            extrude(context, id + "F15", {"entities" : qUnion([Q0, Q1]), "operationType" : NewBodyOperationType.ADD, "surfaceOperationType" : NewSurfaceOperationType.ADD, "surfaceEntities" : qUnion([Q2]), "depth" : (7 + 3.5) * mm, "offsetDistance" : 25 * mm});
        }
        {
            var Q0;
            Q0=makeQuery(id+"F12.imprint","IMPRINT",FACE,{"disambiguationData":[TD([[makeQuery(id+"F12.imprint","IMPRINT",EDGE,{"derivedFrom":sQuery(id+"F12.wireOp",EDGE,"E20")}),1.0]])]});
            var Q1;
            Q1=makeQuery(id+"F12.imprint","IMPRINT",FACE,{"disambiguationData":[TD([[makeQuery(id+"F12.imprint","IMPRINT",EDGE,{"derivedFrom":sQuery(id+"F12.wireOp",EDGE,"E21")}),1.0]])]});
            var Q2;
            Q2=makeQuery(id+"F12.imprint","IMPRINT",FACE,{"disambiguationData":[TD([[makeQuery(id+"F12.imprint","IMPRINT",EDGE,{"derivedFrom":sQuery(id+"F12.wireOp",EDGE,"E24")}),1.0]])]});
            extrude(context, id + "F16", {"entities" : qUnion([Q0, Q1, Q2]), "operationType" : NewBodyOperationType.ADD, "depth" : 7 * mm, "offsetDistance" : 25 * mm});
        }
        {
            var Q0;
            Q0=makeQuery(id+"F2.opExtrude","SWEPT_BODY",BODY,{"disambiguationData":[OSD([sQuery(id+"F0.wireOp",EDGE,"E1"),sQuery(id+"F0.wireOp",EDGE,"E2.right"),sQuery(id+"F0.wireOp",EDGE,"E3.2"),sQuery(id+"F0.wireOp",EDGE,"E10")])]});
            var Q1;
            Q1=sQuery(id+"F0.wireOp",EDGE,"E0");
            circularPattern(context, id + "F17", {"entities" : qUnion([Q0]), "axis" : qUnion([Q1]), "angle" : 120 * degree, "instanceCount" : 3, "oppositeDirection" : true});
        }
        {
            var Q0;
            Q0=makeQuery(id+"F10.imprint","IMPRINT",FACE,{"disambiguationData":[TD([[makeQuery(id+"F10.imprint","IMPRINT",EDGE,{"derivedFrom":sQuery(id+"F10.wireOp",EDGE,"E13")}),-1.0]])]});
            extrude(context, id + "F18", {"entities" : qUnion([Q0]), "operationType" : NewBodyOperationType.ADD, "oppositeDirection" : true, "depth" : 3.5 * mm, "offsetDistance" : 25 * mm});
        }
        {
            var Q0;
            Q0=makeQuery(id+"F12.imprint","IMPRINT",FACE,{"disambiguationData":[TD([[makeQuery(id+"F12.imprint","IMPRINT",EDGE,{"derivedFrom":sQuery(id+"F12.wireOp",EDGE,"E20")}),-1.0]])]});
            extrude(context, id + "F19", {"entities" : qUnion([Q0]), "operationType" : NewBodyOperationType.ADD, "depth" : 3.5 * mm, "offsetDistance" : 25 * mm});
        }
    });
